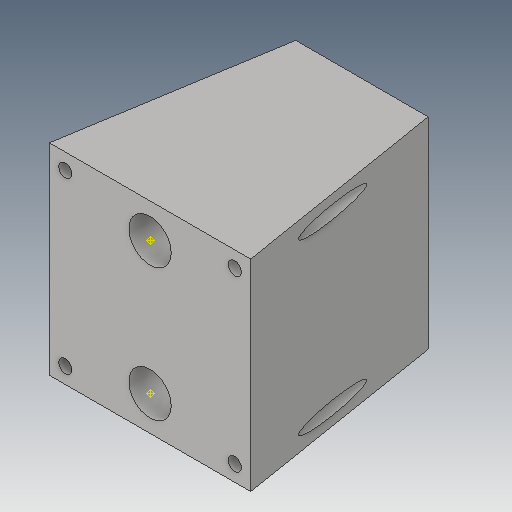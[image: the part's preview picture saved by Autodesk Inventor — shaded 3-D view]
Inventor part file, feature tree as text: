
AUTODESK INVENTOR PART (.ipt)
format: ipt  version: 2019 (Build 230136000, 136)  size: 144,896 bytes
history: native  units: mm
features: hole x3, sketch x3, extrude x2, other x2
ambient origin geometry x8: Origin, YZ Plane, XZ Plane, XY Plane, X Axis, Y Axis, Z Axis, Center Point
bodies: Solid1 (feature_tree)
feature tree (10):
  extrude  "Extrusion1"  Depth=38.0mm
  extrude  "Extrusion2"  Depth=4.2mm
  hole  "Hole1"  [1 undecoded]
  other  "Work Point1"
  other  "Work Point2"
  hole  "Hole2"  [1 undecoded]
  hole  "Hole3"  [1 undecoded]
  sketch  "Sketch1"  dims[d0=25.0mm d1=38.0mm]
  sketch  "Sketch2"  dims[d2=4.2mm d3=4.2mm]
  sketch  "Sketch3"  dims[d4=12.5mm d5=12.5mm d6=40.0mm d7=0.0mm d8=6.5mm d9=6.5mm d10=30.0mm d11=0.0mm d12=16.0mm d13=16.0mm d14=20.0mm d16=32.0mm d17=20.0mm d19=32.0mm d22=2.5mm d23=6.0mm d24=4.0mm d25=2.0mm d26=90.0deg d27=20.0mm d28=20.594885mm d51=10.0mm d52=10.0mm d31=8.0mm d32=6.0mm d33=4.0mm d34=2.0mm d35=90.0deg d36=36.0mm d37=20.594885mm d47=10.0mm d48=10.0mm d40=8.0mm d41=6.0mm d42=4.0mm d43=2.0mm d44=90.0deg d45=36.0mm d46=20.594885mm]
note: 3 required parameter values undecoded (feature->parameter linkage not recoverable at this tier; creation-order binding heuristic only, values carry confidence <= 0.55)
